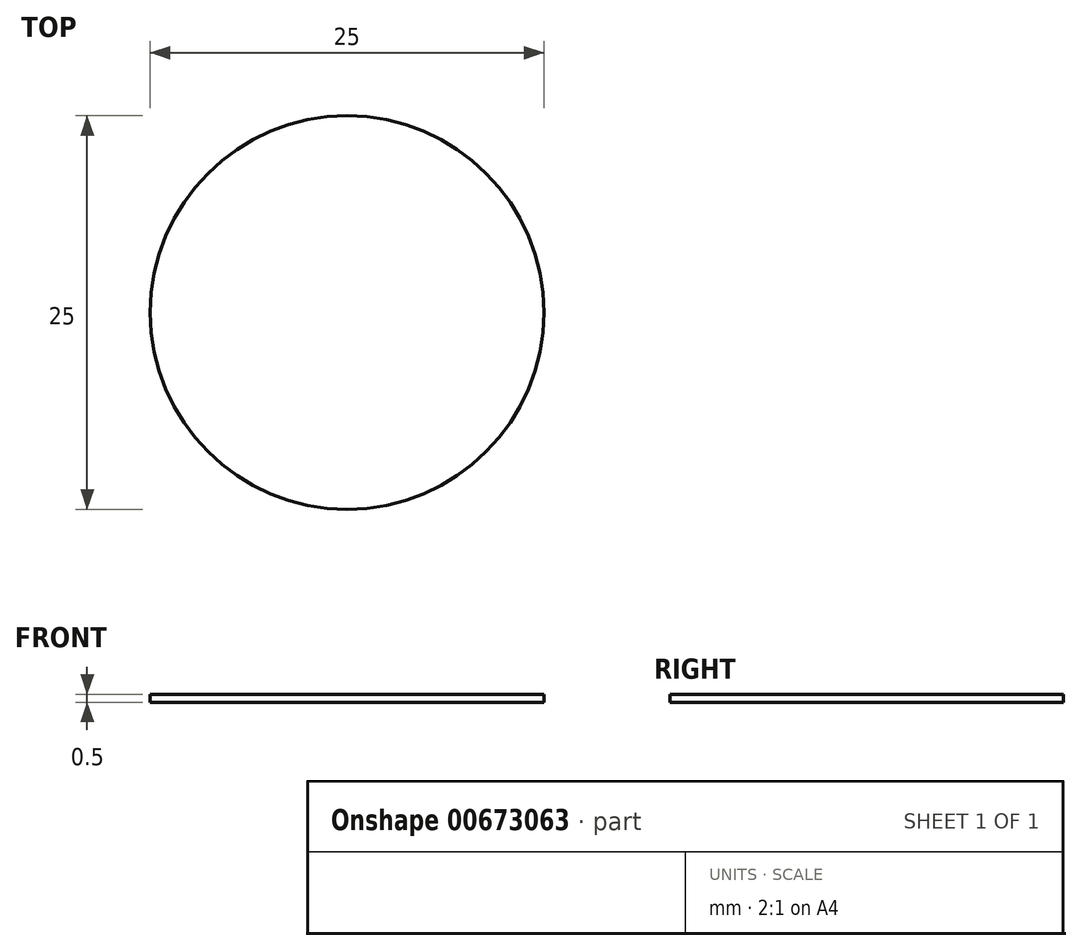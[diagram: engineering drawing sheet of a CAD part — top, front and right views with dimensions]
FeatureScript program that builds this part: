
annotation { "Feature Type Name" : "Feature", "Feature Type Description" : "" }
export const myFeature = defineFeature(function(context is Context, id is Id, definition is map)
    precondition{}
    {
        {
            var Q0;
            Q0=qCreatedBy(makeId("Top.planeOp"),FACE);
            var sketch = newSketch(context, id + "F0", { "sketchPlane" : qUnion([Q0])});
            skCircle(sketch, "E0", {"center": v(0, 0) * mm, "radius": 12.5 * mm});
            skSolve(sketch);
        }
        {
            var Q0;
            Q0 = qSketchRegion(id + "F0", true);
            extrude(context, id + "F1", {"entities" : qUnion([Q0]), "depth" : 0.5 * mm, "offsetDistance" : 25 * mm});
        }
    });
